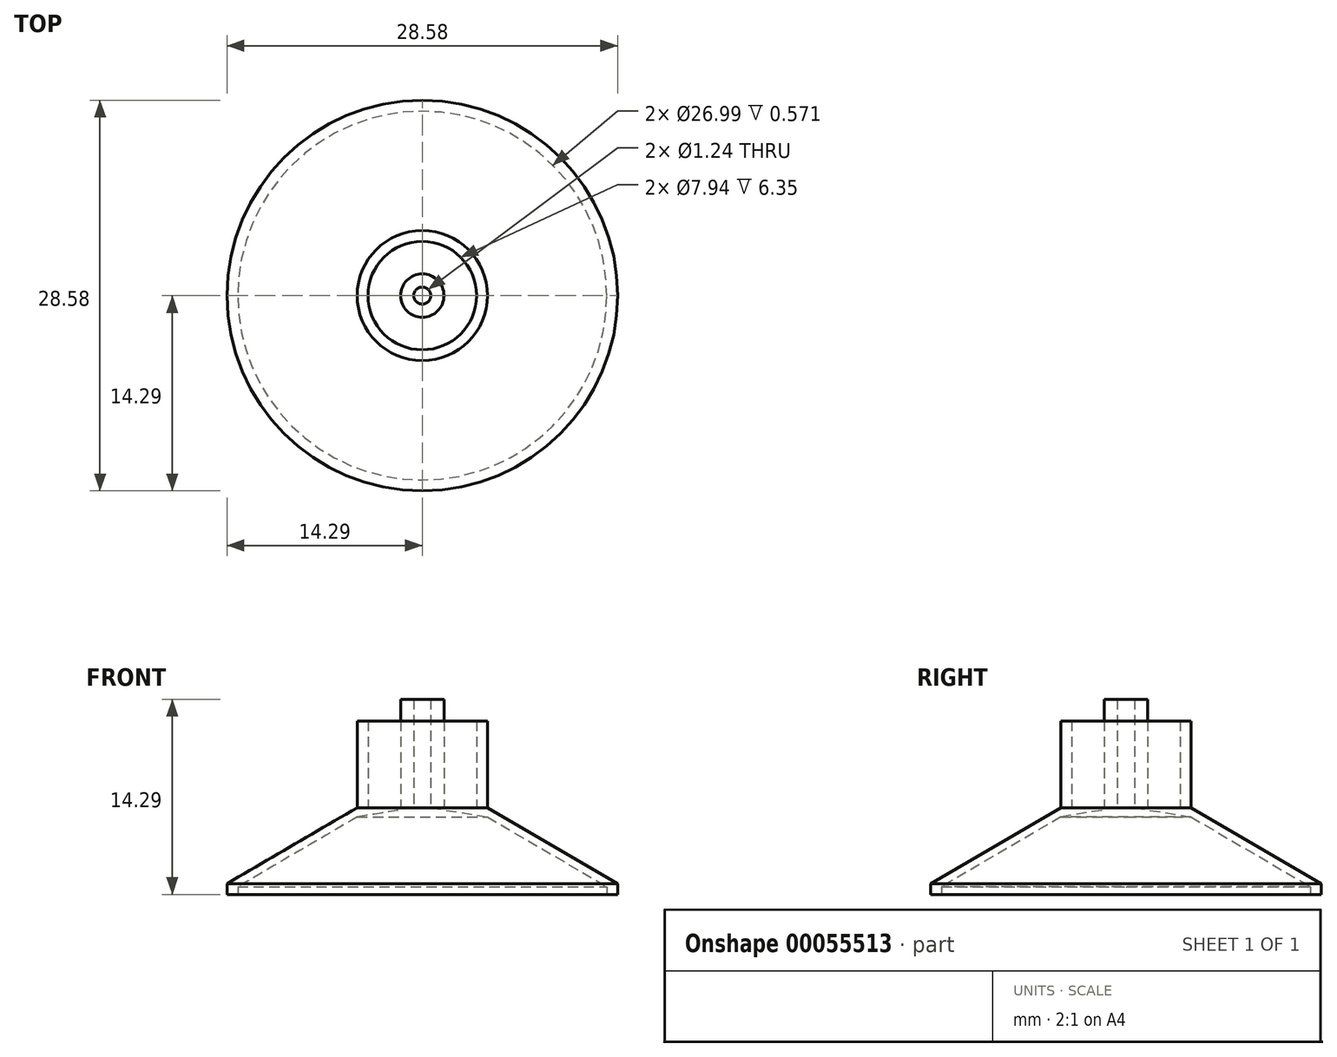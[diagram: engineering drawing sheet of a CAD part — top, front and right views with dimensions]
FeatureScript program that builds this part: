
annotation { "Feature Type Name" : "Feature", "Feature Type Description" : "" }
export const myFeature = defineFeature(function(context is Context, id is Id, definition is map)
    precondition{}
    {
        {
            var Q0;
            Q0=qCreatedBy(makeId("Right.planeOp"),FACE);
            var sketch = newSketch(context, id + "F0", { "sketchPlane" : qUnion([Q0])});
            skLineSegment(sketch, "E0", {"start": v(-7.94, -10.27) * mm, "end": v(-7.94, -3.92) * mm, "construction": true});
            skLineSegment(sketch, "E1", {"start": v(-22.23, -10.27) * mm, "end": v(-22.23, -9.48) * mm});
            skLineSegment(sketch, "E2", {"start": v(-22.23, -9.48) * mm, "end": v(-12.7, -3.92) * mm});
            skLineSegment(sketch, "E3.MirrorCS", {"start": v(6.35, -9.48) * mm, "end": v(-3.18, -3.92) * mm});
            skLineSegment(sketch, "E4.MirrorCS", {"start": v(6.35, -10.27) * mm, "end": v(6.35, -9.48) * mm});
            skLineSegment(sketch, "E5", {"start": v(-12.7, -3.92) * mm, "end": v(-12.7, 2.43) * mm});
            skLineSegment(sketch, "E6", {"start": v(-3.18, -3.92) * mm, "end": v(-3.18, 2.43) * mm});
            skLineSegment(sketch, "E7", {"start": v(-12.7, 2.43) * mm, "end": v(-11.9, 2.43) * mm});
            skLineSegment(sketch, "E8", {"start": v(-11.9, 2.43) * mm, "end": v(-11.9, -3.92) * mm});
            skLineSegment(sketch, "E9", {"start": v(-7.94, -3.92) * mm, "end": v(-7.94, 4.33) * mm, "construction": true});
            skLineSegment(sketch, "E10.MirrorCS", {"start": v(-3.97, 2.43) * mm, "end": v(-3.97, -3.92) * mm});
            skLineSegment(sketch, "E11.MirrorCS", {"start": v(-3.18, 2.43) * mm, "end": v(-3.97, 2.43) * mm});
            skLineSegment(sketch, "E12", {"start": v(-22.23, -10.27) * mm, "end": v(-21.43, -10.27) * mm});
            skLineSegment(sketch, "E13", {"start": v(-21.43, -10.27) * mm, "end": v(-21.43, -9.7) * mm});
            skLineSegment(sketch, "E14", {"start": v(-21.43, -9.7) * mm, "end": v(-12.7, -4.6) * mm});
            skLineSegment(sketch, "E15.MirrorCS", {"start": v(5.55, -10.27) * mm, "end": v(5.55, -9.7) * mm});
            skLineSegment(sketch, "E16.MirrorCS", {"start": v(6.35, -10.27) * mm, "end": v(5.55, -10.27) * mm});
            skLineSegment(sketch, "E17.MirrorCS", {"start": v(5.55, -9.7) * mm, "end": v(-3.18, -4.6) * mm});
            skLineSegment(sketch, "E18.trimOffspring", {"start": v(-6.35, -3.92) * mm, "end": v(-3.97, -3.92) * mm});
            skLineSegment(sketch, "E19.trimOffspring", {"start": v(-9.53, -3.92) * mm, "end": v(-11.9, -3.92) * mm});
            skLineSegment(sketch, "E20", {"start": v(-9.53, -3.92) * mm, "end": v(-9.53, 4.02) * mm});
            skLineSegment(sketch, "E21.MirrorCS", {"start": v(-6.35, -3.92) * mm, "end": v(-6.35, 4.02) * mm});
            skLineSegment(sketch, "E22", {"start": v(-9.53, 4.02) * mm, "end": v(-8.56, 4.02) * mm});
            skLineSegment(sketch, "E23.MirrorCS", {"start": v(-6.35, 4.02) * mm, "end": v(-7.32, 4.02) * mm});
            skLineSegment(sketch, "E24", {"start": v(-8.56, 4.02) * mm, "end": v(-8.56, -3.92) * mm});
            skLineSegment(sketch, "E25.MirrorCS", {"start": v(-7.32, 4.02) * mm, "end": v(-7.32, -3.92) * mm});
            skLineSegment(sketch, "E26", {"start": v(-12.7, -4.6) * mm, "end": v(-8.56, -3.92) * mm});
            skLineSegment(sketch, "E27", {"start": v(-7.32, -3.92) * mm, "end": v(-3.18, -4.6) * mm});
            skSolve(sketch);
        }
        {
            var Q0;
            Q0 = qSketchRegion(id + "F0", true);
            var Q1;
            Q1=sQuery(id+"F0.wireOp",EDGE,"E0");
            revolve(context, id + "F1", {"entities" : qUnion([Q0]), "axis" : qUnion([Q1]), "revolveType" : RevolveType.FULL});
        }
    });
